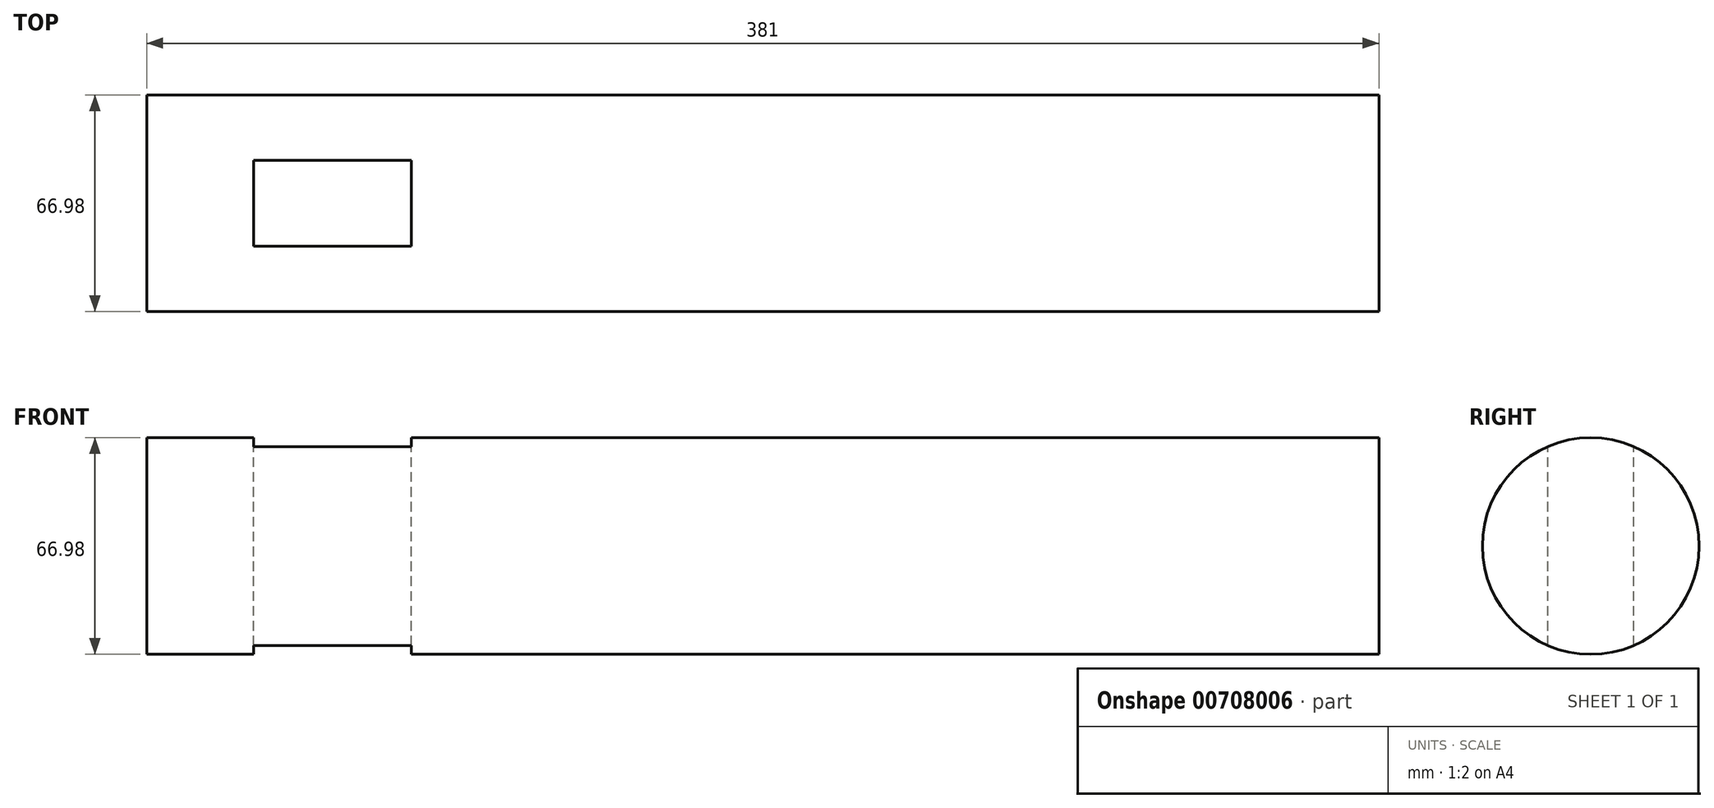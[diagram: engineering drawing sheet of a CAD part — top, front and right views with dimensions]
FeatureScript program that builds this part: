
annotation { "Feature Type Name" : "Feature", "Feature Type Description" : "" }
export const myFeature = defineFeature(function(context is Context, id is Id, definition is map)
    precondition{}
    {
        {
            var Q0;
            Q0=qCreatedBy(makeId("Right.planeOp"),FACE);
            var sketch = newSketch(context, id + "F0", { "sketchPlane" : qUnion([Q0])});
            skCircle(sketch, "E0", {"center": v(0, 0) * mm, "radius": 33.49 * mm});
            skSolve(sketch);
        }
        {
            var Q0;
            Q0=makeQuery(id+"F0.imprint","IMPRINT",FACE,{"disambiguationData":[TD([[makeQuery(id+"F0.imprint","IMPRINT",EDGE,{"derivedFrom":sQuery(id+"F0.wireOp",EDGE,"E0")}),1.0]])]});
            extrude(context, id + "F1", {"entities" : qUnion([Q0]), "endBound" : BoundingType.SYMMETRIC, "depth" : 381 * mm, "offsetDistance" : 25.4 * mm});
        }
        {
            var Q0;
            Q0=qCreatedBy(makeId("Top.planeOp"),FACE);
            var sketch = newSketch(context, id + "F2", { "sketchPlane" : qUnion([Q0])});
            skLineSegment(sketch, "E1.bottom", {"start": v(-108.69, 13.25) * mm, "end": v(-157.46, 13.25) * mm});
            skLineSegment(sketch, "E1.top", {"start": v(-108.69, -13.25) * mm, "end": v(-157.46, -13.25) * mm});
            skLineSegment(sketch, "E1.left", {"start": v(-108.69, 13.25) * mm, "end": v(-108.69, -13.25) * mm});
            skLineSegment(sketch, "E1.right", {"start": v(-157.46, 13.25) * mm, "end": v(-157.46, -13.25) * mm});
            skPoint(sketch, "E1.middle", {"position": v(-133.07, 0) * mm});
            skSolve(sketch);
        }
        {
            var Q0;
            Q0 = qSketchRegion(id + "F2", true);
            extrude(context, id + "F3", {"entities" : qUnion([Q0]), "operationType" : NewBodyOperationType.REMOVE, "endBound" : BoundingType.SYMMETRIC, "oppositeDirection" : true, "depth" : 127 * mm, "offsetDistance" : 25.4 * mm});
        }
    });
